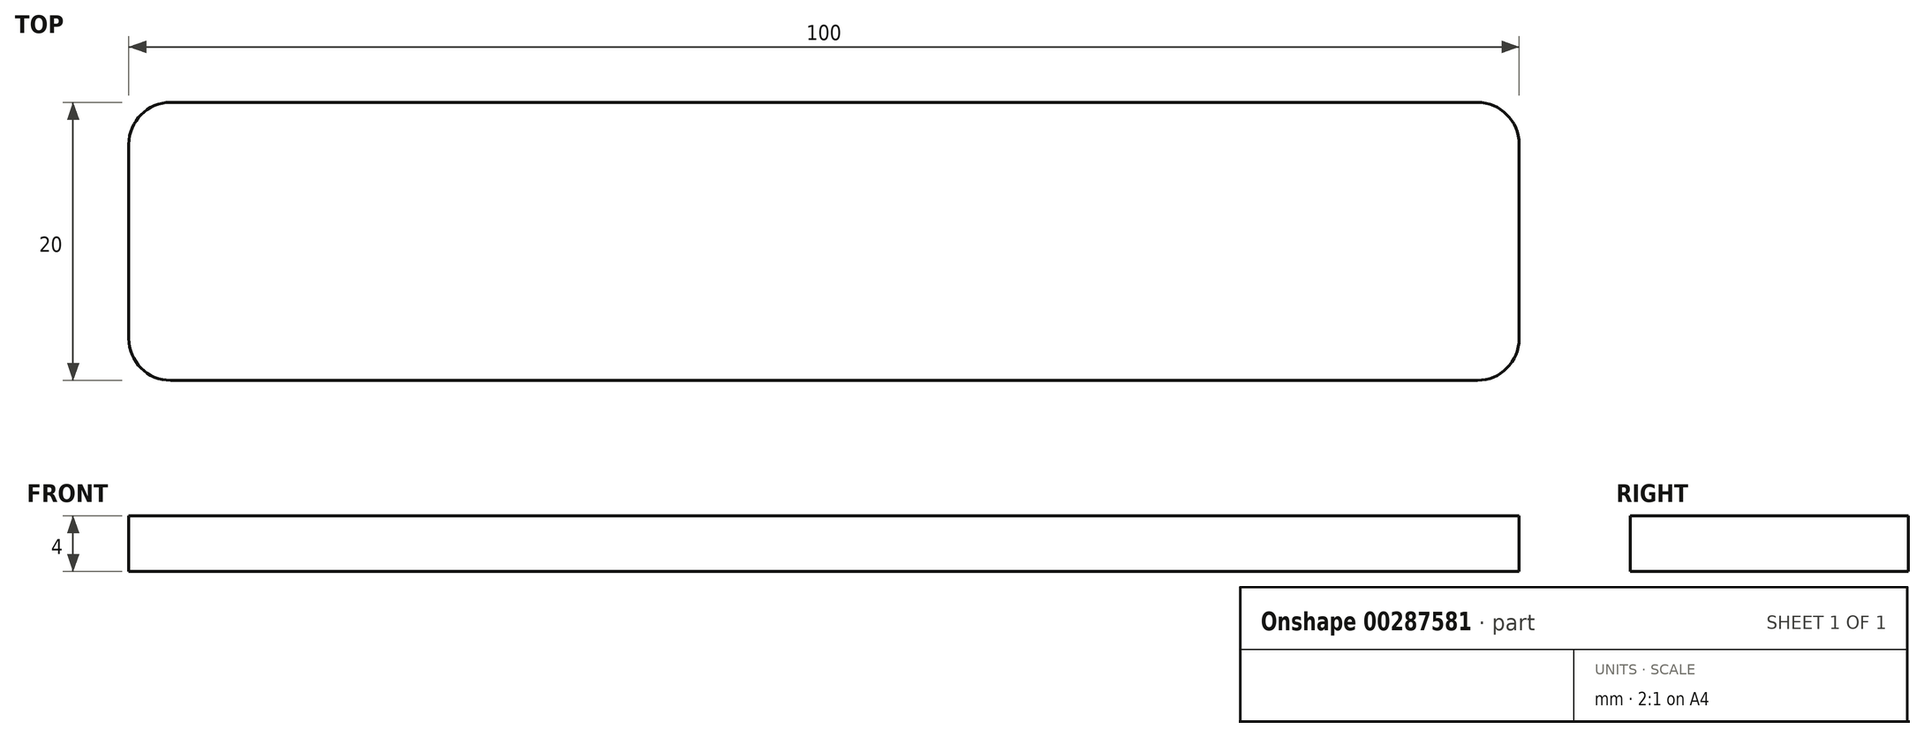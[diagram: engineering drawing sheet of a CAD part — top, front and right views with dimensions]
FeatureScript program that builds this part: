
annotation { "Feature Type Name" : "Feature", "Feature Type Description" : "" }
export const myFeature = defineFeature(function(context is Context, id is Id, definition is map)
    precondition{}
    {
        {
            var Q0;
            Q0=qCreatedBy(makeId("Top.planeOp"),FACE);
            var sketch = newSketch(context, id + "F0", { "sketchPlane" : qUnion([Q0])});
            skLineSegment(sketch, "E0.bottom", {"start": v(47, -10) * mm, "end": v(-47, -10) * mm});
            skLineSegment(sketch, "E0.top", {"start": v(47, 10) * mm, "end": v(-47, 10) * mm});
            skLineSegment(sketch, "E0.left", {"start": v(50, -7) * mm, "end": v(50, 7) * mm});
            skLineSegment(sketch, "E0.right", {"start": v(-50, -7) * mm, "end": v(-50, 7) * mm});
            skPoint(sketch, "E0.middle", {"position": v(0, 0) * mm});
            skPoint(sketch, "E1.visualSharp", {"position": v(-50, 10) * mm});
            skArc(sketch, "E1.filletArc", {"start": v(-47, 10) * mm, "mid": v(-49.12, 9.12) * mm, "end": v(-50, 7) * mm});
            skPoint(sketch, "E2.visualSharp", {"position": v(-50, -10) * mm});
            skArc(sketch, "E2.filletArc", {"start": v(-50, -7) * mm, "mid": v(-49.12, -9.12) * mm, "end": v(-47, -10) * mm});
            skPoint(sketch, "E3.visualSharp", {"position": v(50, -10) * mm});
            skArc(sketch, "E3.filletArc", {"start": v(47, -10) * mm, "mid": v(49.12, -9.12) * mm, "end": v(50, -7) * mm});
            skPoint(sketch, "E4.visualSharp", {"position": v(50, 10) * mm});
            skArc(sketch, "E4.filletArc", {"start": v(50, 7) * mm, "mid": v(49.12, 9.12) * mm, "end": v(47, 10) * mm});
            skSolve(sketch);
        }
        {
            var Q0;
            Q0=makeQuery(id+"F0.imprint","IMPRINT",FACE,{"disambiguationData":[TD([[makeQuery(id+"F0.imprint","IMPRINT",EDGE,{"derivedFrom":sQuery(id+"F0.wireOp",EDGE,"E0.bottom")}),-1.0]])]});
            extrude(context, id + "F1", {"entities" : qUnion([Q0]), "depth" : 4 * mm});
        }
    });
